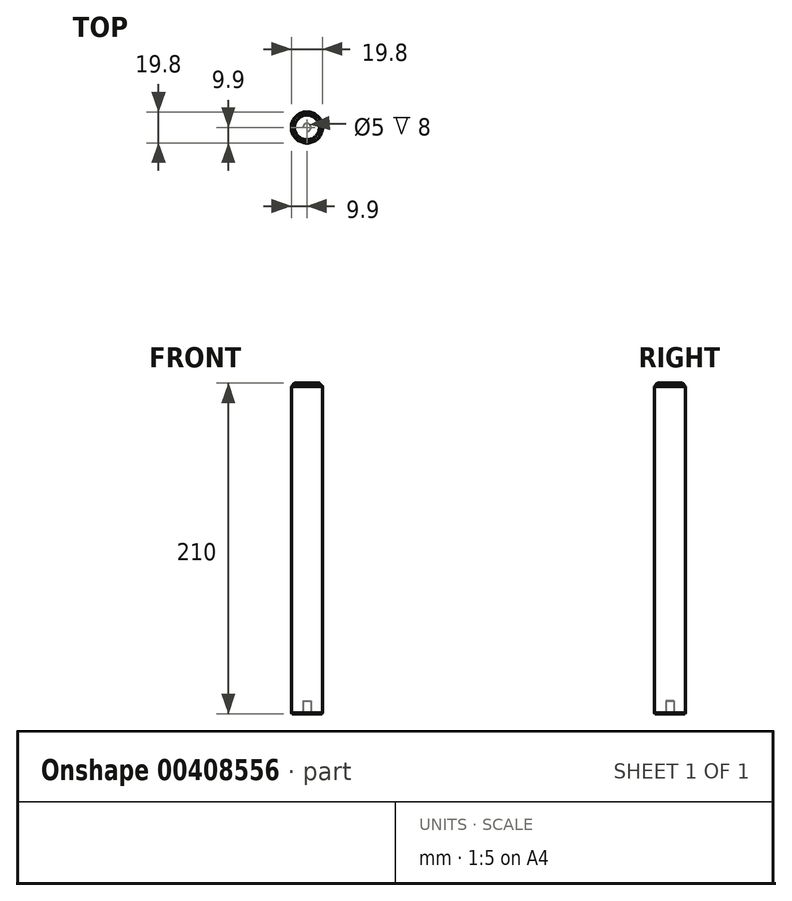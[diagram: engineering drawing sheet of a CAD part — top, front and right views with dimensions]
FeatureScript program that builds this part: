
annotation { "Feature Type Name" : "Feature", "Feature Type Description" : "" }
export const myFeature = defineFeature(function(context is Context, id is Id, definition is map)
    precondition{}
    {
        {
            var Q0;
            Q0=qCreatedBy(makeId("Top.planeOp"),FACE);
            var sketch = newSketch(context, id + "F0", { "sketchPlane" : qUnion([Q0])});
            skCircle(sketch, "E0", {"center": v(0, 0) * mm, "radius": 9.9 * mm});
            skSolve(sketch);
        }
        {
            var Q0;
            Q0 = qSketchRegion(id + "F0", true);
            extrude(context, id + "F1", {"entities" : qUnion([Q0]), "depth" : 210 * mm});
        }
        {
            var Q0;
            Q0=makeQuery(id+"F1.opExtrude","CAP_EDGE",EDGE,{"disambiguationData":[OSD([sQuery(id+"F0.wireOp",EDGE,"E0")])],"isStart":false});
            chamfer(context, id + "F2", {"entities" : qUnion([Q0]), "width" : 2 * mm, "tangentPropagation" : true});
        }
        {
            var Q0;
            Q0=makeQuery(id+"F1.opExtrude","CAP_FACE",FACE,{"disambiguationData":[OSD([sQuery(id+"F0.wireOp",EDGE,"E0")])],"isStart":true});
            var sketch = newSketch(context, id + "F3", { "sketchPlane" : qUnion([Q0])});
            skCircle(sketch, "E1", {"center": v(0, 0) * mm, "radius": 2.5 * mm});
            skSolve(sketch);
        }
        {
            var Q0;
            Q0=makeQuery(id+"F3.imprint","IMPRINT",FACE,{"disambiguationData":[TD([[makeQuery(id+"F3.imprint","IMPRINT",EDGE,{"derivedFrom":sQuery(id+"F3.wireOp",EDGE,"E1")}),1.0]])]});
            var Q1;
            Q1=sQuery(id+"F3.wireOp",EDGE,"E1");
            extrude(context, id + "F4", {"entities" : qUnion([Q0]), "operationType" : NewBodyOperationType.REMOVE, "surfaceEntities" : qUnion([Q1]), "oppositeDirection" : true, "depth" : 8 * mm});
        }
        {
            var Q0;
            Q0=makeQuery(id+"F1.opExtrude","CAP_EDGE",EDGE,{"disambiguationData":[OSD([sQuery(id+"F0.wireOp",EDGE,"E0")])],"isStart":true});
            chamfer(context, id + "F5", {"entities" : qUnion([Q0]), "width" : 0.5 * mm, "tangentPropagation" : true});
        }
    });
